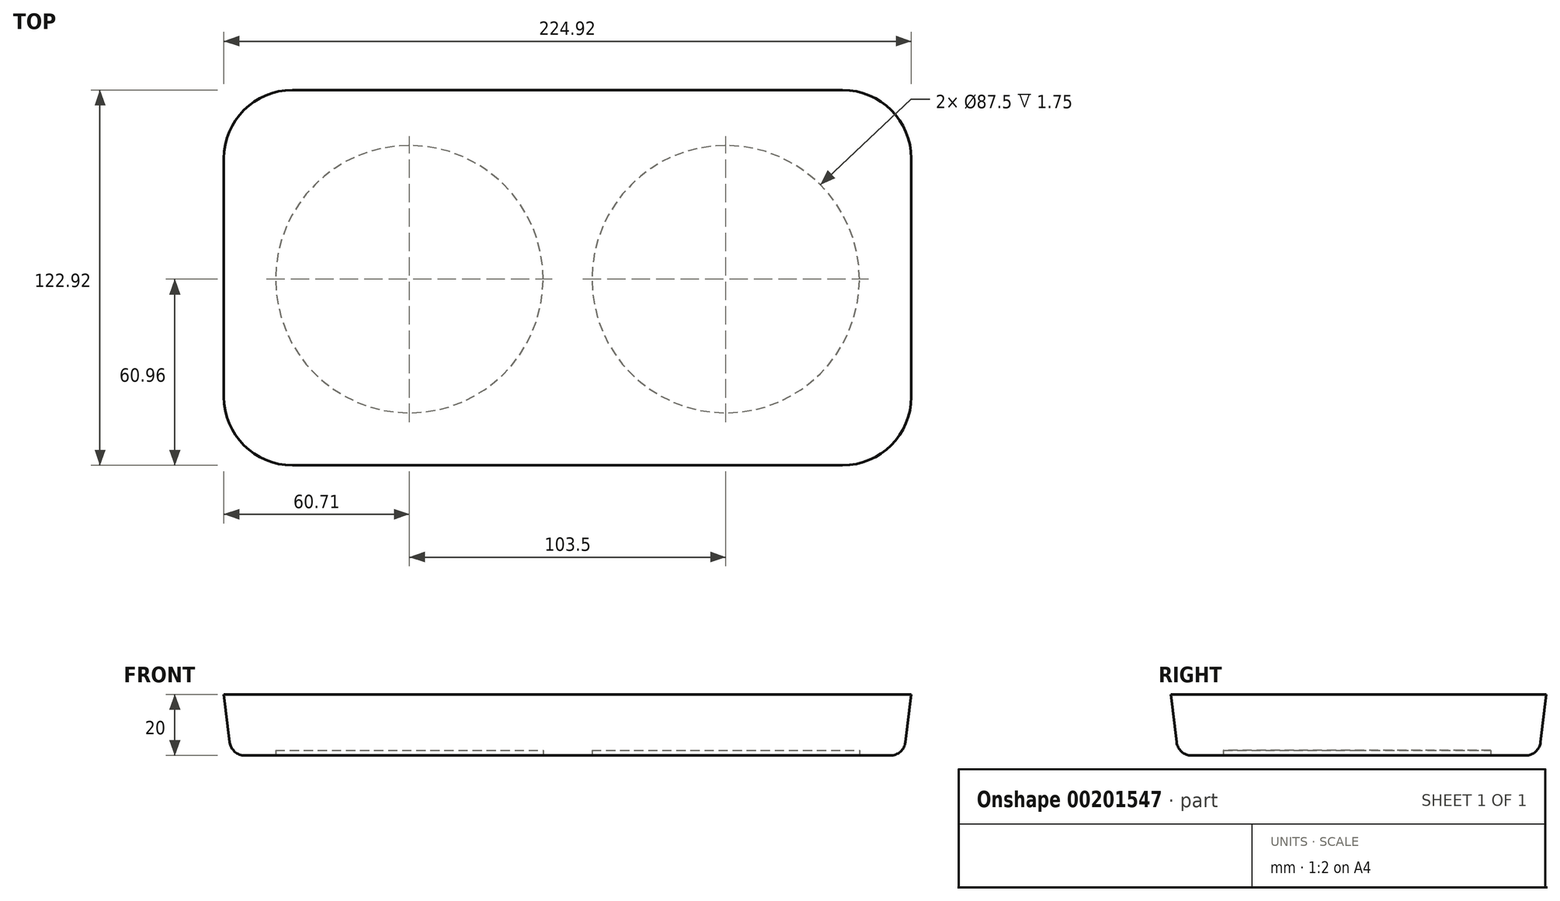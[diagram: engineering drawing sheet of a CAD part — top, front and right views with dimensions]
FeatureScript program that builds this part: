
annotation { "Feature Type Name" : "Feature", "Feature Type Description" : "" }
export const myFeature = defineFeature(function(context is Context, id is Id, definition is map)
    precondition{}
    {
        {
            var Q0;
            Q0=qCreatedBy(makeId("Top.planeOp"),FACE);
            var sketch = newSketch(context, id + "F0", { "sketchPlane" : qUnion([Q0])});
            skLineSegment(sketch, "E0.bottom", {"start": v(20, 0) * mm, "end": v(200, 0) * mm});
            skLineSegment(sketch, "E0.top", {"start": v(20, 118) * mm, "end": v(200, 118) * mm});
            skLineSegment(sketch, "E0.left", {"start": v(0, 20) * mm, "end": v(0, 98) * mm});
            skLineSegment(sketch, "E0.right", {"start": v(220, 20) * mm, "end": v(220, 98) * mm});
            skPoint(sketch, "E1.visualSharp", {"position": v(0, 118) * mm});
            skArc(sketch, "E1.filletArc", {"start": v(20, 118) * mm, "mid": v(5.86, 112.14) * mm, "end": v(0, 98) * mm});
            skPoint(sketch, "E2.visualSharp", {"position": v(220, 118) * mm});
            skArc(sketch, "E2.filletArc", {"start": v(220, 98) * mm, "mid": v(214.14, 112.14) * mm, "end": v(200, 118) * mm});
            skPoint(sketch, "E3.visualSharp", {"position": v(0, 0) * mm});
            skArc(sketch, "E3.filletArc", {"start": v(0, 20) * mm, "mid": v(5.86, 5.86) * mm, "end": v(20, 0) * mm});
            skPoint(sketch, "E4.visualSharp", {"position": v(220, 0) * mm});
            skArc(sketch, "E4.filletArc", {"start": v(200, 0) * mm, "mid": v(214.14, 5.86) * mm, "end": v(220, 20) * mm});
            skSolve(sketch);
        }
        {
            var Q0;
            Q0=makeQuery(id+"F0.imprint","IMPRINT",FACE,{"disambiguationData":[TD([[makeQuery(id+"F0.imprint","IMPRINT",EDGE,{"derivedFrom":sQuery(id+"F0.wireOp",EDGE,"E0.bottom")}),1.0]])]});
            extrude(context, id + "F1", {"entities" : qUnion([Q0]), "depth" : 20 * mm, "hasDraft" : true, "draftAngle" : 7 * degree});
        }
        {
            var Q0;
            Q0=makeQuery(id+"F1.opExtrude","CAP_FACE",FACE,{"disambiguationData":[OSD([sQuery(id+"F0.wireOp",EDGE,"E0.bottom"),sQuery(id+"F0.wireOp",EDGE,"E0.top"),sQuery(id+"F0.wireOp",EDGE,"E0.left"),sQuery(id+"F0.wireOp",EDGE,"E0.right"),sQuery(id+"F0.wireOp",EDGE,"E1.filletArc"),sQuery(id+"F0.wireOp",EDGE,"E2.filletArc"),sQuery(id+"F0.wireOp",EDGE,"E3.filletArc"),sQuery(id+"F0.wireOp",EDGE,"E4.filletArc")])],"isStart":true});
            fillet(context, id + "F2", {"entities" : qUnion([Q0]), "radius" : 5 * mm, "tangentPropagation" : true, "allowEdgeOverflow" : false});
        }
        {
            var Q0;
            Q0=makeQuery(id+"F1.opExtrude","CAP_FACE",FACE,{"disambiguationData":[OSD([sQuery(id+"F0.wireOp",EDGE,"E0.bottom"),sQuery(id+"F0.wireOp",EDGE,"E0.top"),sQuery(id+"F0.wireOp",EDGE,"E0.left"),sQuery(id+"F0.wireOp",EDGE,"E0.right"),sQuery(id+"F0.wireOp",EDGE,"E1.filletArc"),sQuery(id+"F0.wireOp",EDGE,"E2.filletArc"),sQuery(id+"F0.wireOp",EDGE,"E3.filletArc"),sQuery(id+"F0.wireOp",EDGE,"E4.filletArc")])],"isStart":true});
            var sketch = newSketch(context, id + "F3", { "sketchPlane" : qUnion([Q0])});
            skLineSegment(sketch, "E5.bottom", {"start": v(0, 0) * mm, "end": v(58.25, 0) * mm, "construction": true});
            skLineSegment(sketch, "E5.top", {"start": v(0, -58.5) * mm, "end": v(58.25, -58.5) * mm, "construction": true});
            skLineSegment(sketch, "E5.left", {"start": v(0, 0) * mm, "end": v(0, -58.5) * mm, "construction": true});
            skLineSegment(sketch, "E5.right", {"start": v(58.25, 0) * mm, "end": v(58.25, -58.5) * mm, "construction": true});
            skLineSegment(sketch, "E6.bottom", {"start": v(0, 0) * mm, "end": v(161.75, 0) * mm, "construction": true});
            skLineSegment(sketch, "E6.top", {"start": v(0, -58.5) * mm, "end": v(161.75, -58.5) * mm, "construction": true});
            skLineSegment(sketch, "E6.right", {"start": v(161.75, 0) * mm, "end": v(161.75, -58.5) * mm, "construction": true});
            skCircle(sketch, "E7", {"center": v(58.25, -58.5) * mm, "radius": 43.75 * mm});
            skCircle(sketch, "E8", {"center": v(161.75, -58.5) * mm, "radius": 43.75 * mm});
            skSolve(sketch);
        }
        {
            var Q0;
            Q0=qSketchRegion(id+"F3",true);
            extrude(context, id + "F4", {"entities" : qUnion([Q0]), "operationType" : NewBodyOperationType.REMOVE, "oppositeDirection" : true, "depth" : 1.75 * mm});
        }
    });
